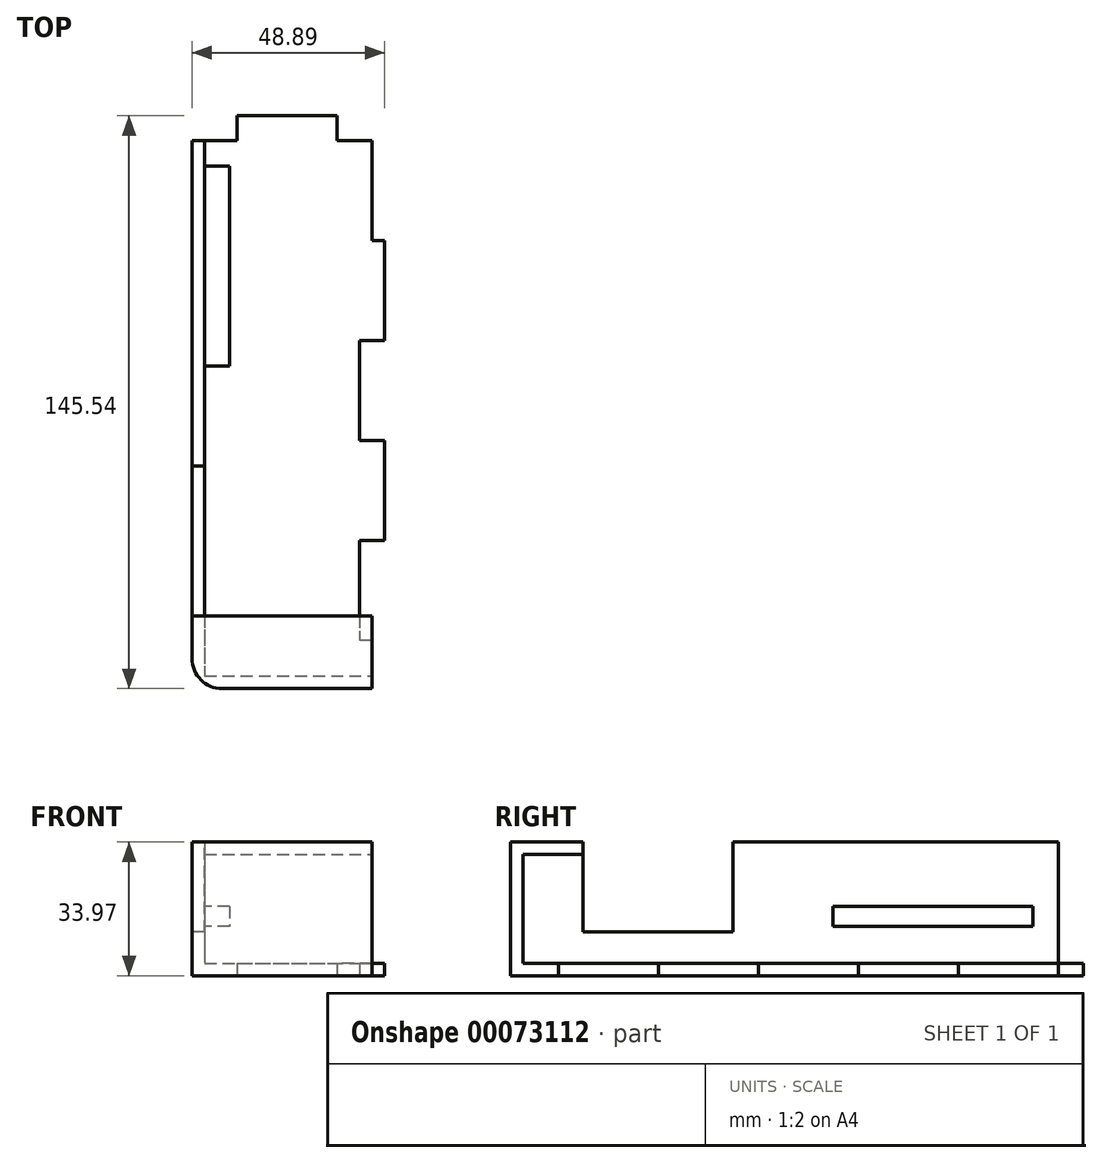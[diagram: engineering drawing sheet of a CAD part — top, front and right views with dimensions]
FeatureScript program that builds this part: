
annotation { "Feature Type Name" : "Feature", "Feature Type Description" : "" }
export const myFeature = defineFeature(function(context is Context, id is Id, definition is map)
    precondition{}
    {
        {
            var Q0;
            Q0=qCreatedBy(makeId("Top.planeOp"),FACE);
            var sketch = newSketch(context, id + "F0", { "sketchPlane" : qUnion([Q0])});
            skLineSegment(sketch, "E0.bottom", {"start": v(-32.54, 107.25) * mm, "end": v(-21.11, 107.25) * mm});
            skLineSegment(sketch, "E0.top", {"start": v(-32.54, -31.94) * mm, "end": v(13.18, -31.94) * mm});
            skLineSegment(sketch, "E0.left", {"start": v(-32.54, 107.25) * mm, "end": v(-32.54, -31.94) * mm});
            skLineSegment(sketch, "E1.bottom", {"start": v(13.18, 107.25) * mm, "end": v(10, 107.25) * mm});
            skLineSegment(sketch, "E1.top", {"start": v(13.18, 81.85) * mm, "end": v(10, 81.85) * mm});
            skLineSegment(sketch, "E2.0.1.0", {"start": v(13.18, 56.45) * mm, "end": v(10, 56.45) * mm});
            skLineSegment(sketch, "E2.0.1.1", {"start": v(10, 56.45) * mm, "end": v(10, 31.05) * mm});
            skLineSegment(sketch, "E2.0.1.2", {"start": v(13.18, 31.05) * mm, "end": v(10, 31.05) * mm});
            skLineSegment(sketch, "E2.0.2.0", {"start": v(13.18, 5.65) * mm, "end": v(10, 5.65) * mm});
            skLineSegment(sketch, "E2.0.2.1", {"start": v(10, 5.65) * mm, "end": v(10, -19.75) * mm});
            skLineSegment(sketch, "E2.0.2.2", {"start": v(13.18, -19.75) * mm, "end": v(10, -19.75) * mm});
            skLineSegment(sketch, "E2.direction1", {"start": v(10, 94.55) * mm, "end": v(35.4, 94.55) * mm, "construction": true});
            skLineSegment(sketch, "E2.direction2", {"start": v(10, 94.55) * mm, "end": v(10, 43.75) * mm, "construction": true});
            skLineSegment(sketch, "E3.bottom", {"start": v(13.18, 81.85) * mm, "end": v(16.35, 81.85) * mm});
            skLineSegment(sketch, "E3.top", {"start": v(13.18, 56.45) * mm, "end": v(16.35, 56.45) * mm});
            skLineSegment(sketch, "E3.right", {"start": v(16.35, 81.85) * mm, "end": v(16.35, 56.45) * mm});
            skLineSegment(sketch, "E4.0.1.0", {"start": v(13.18, 31.05) * mm, "end": v(16.35, 31.05) * mm});
            skLineSegment(sketch, "E4.0.1.1", {"start": v(16.35, 31.05) * mm, "end": v(16.35, 5.65) * mm});
            skLineSegment(sketch, "E4.0.1.2", {"start": v(13.18, 5.65) * mm, "end": v(16.35, 5.65) * mm});
            skLineSegment(sketch, "E4.direction1", {"start": v(13.18, 81.85) * mm, "end": v(38.58, 81.85) * mm, "construction": true});
            skLineSegment(sketch, "E4.direction2", {"start": v(13.18, 81.85) * mm, "end": v(13.18, 31.05) * mm, "construction": true});
            skLineSegment(sketch, "E5", {"start": v(13.18, 107.25) * mm, "end": v(13.18, 81.85) * mm});
            skLineSegment(sketch, "E6", {"start": v(13.18, -31.94) * mm, "end": v(13.18, -19.75) * mm});
            skLineSegment(sketch, "E7.top", {"start": v(-21.11, 113.6) * mm, "end": v(4.29, 113.6) * mm});
            skLineSegment(sketch, "E7.left", {"start": v(-21.11, 107.25) * mm, "end": v(-21.11, 113.6) * mm});
            skLineSegment(sketch, "E7.right", {"start": v(4.29, 107.25) * mm, "end": v(4.29, 113.6) * mm});
            skLineSegment(sketch, "E8.trimOffspring", {"start": v(4.29, 107.25) * mm, "end": v(13.18, 107.25) * mm});
            skSolve(sketch);
        }
        {
            var Q0;
            Q0=makeQuery(id+"F0.imprint","IMPRINT",FACE,{"disambiguationData":[TD([[makeQuery(id+"F0.imprint","IMPRINT",EDGE,{"derivedFrom":sQuery(id+"F0.wireOp",EDGE,"E0.bottom")}),-1.0]])]});
            extrude(context, id + "F1", {"entities" : qUnion([Q0]), "depth" : 3.17 * mm});
        }
        {
            var Q0;
            Q0=makeQuery(id+"F1.opExtrude","CAP_FACE",FACE,{"disambiguationData":[OSD([sQuery(id+"F0.wireOp",EDGE,"E0.bottom"),sQuery(id+"F0.wireOp",EDGE,"E0.top"),sQuery(id+"F0.wireOp",EDGE,"E0.left"),sQuery(id+"F0.wireOp",EDGE,"E1.top"),sQuery(id+"F0.wireOp",EDGE,"E1.right"),sQuery(id+"F0.wireOp",EDGE,"E2.0.1.0"),sQuery(id+"F0.wireOp",EDGE,"E2.0.1.1"),sQuery(id+"F0.wireOp",EDGE,"E2.0.1.2"),sQuery(id+"F0.wireOp",EDGE,"E2.0.2.0"),sQuery(id+"F0.wireOp",EDGE,"E2.0.2.1"),sQuery(id+"F0.wireOp",EDGE,"E2.0.2.2"),sQuery(id+"F0.wireOp",EDGE,"E2.0.3.0"),sQuery(id+"F0.wireOp",EDGE,"E2.0.3.1"),sQuery(id+"F0.wireOp",EDGE,"E3.bottom"),sQuery(id+"F0.wireOp",EDGE,"E3.top"),sQuery(id+"F0.wireOp",EDGE,"E3.right"),sQuery(id+"F0.wireOp",EDGE,"E4.0.1.0"),sQuery(id+"F0.wireOp",EDGE,"E4.0.1.1"),sQuery(id+"F0.wireOp",EDGE,"E4.0.1.2"),sQuery(id+"F0.wireOp",EDGE,"E4.0.2.0"),sQuery(id+"F0.wireOp",EDGE,"E4.0.2.1"),sQuery(id+"F0.wireOp",EDGE,"E4.0.2.2"),sQuery(id+"F0.wireOp",EDGE,"pYJ3T49I-Cm0M-1mBg-DGMC-QoNwpn64H0FC"),sQuery(id+"F0.wireOp",EDGE,"ms7zWnSc-LKju-jYRc-7B30-AOrHfCOUoyog")])],"isStart":false});
            var sketch = newSketch(context, id + "F2", { "sketchPlane" : qUnion([Q0])});
            skLineSegment(sketch, "E9.0", {"start": v(-29.37, -28.76) * mm, "end": v(13.18, -28.76) * mm});
            skLineSegment(sketch, "E9.1", {"start": v(-29.37, 107.25) * mm, "end": v(-29.37, -28.76) * mm});
            skSolve(sketch);
        }
        {
            var Q0;
            {var subQ2=sQuery(id+"F2.wireOp",EDGE,"E9.1");Q0=makeQuery(id+"F2.imprint","IMPRINT",FACE,{"disambiguationData":[TD([[makeQuery(id+"F2.imprint","IMPRINT",EDGE,{"derivedFrom":subQ2}),-1.0]])]});}
            extrude(context, id + "F3", {"entities" : qUnion([Q0]), "operationType" : NewBodyOperationType.ADD, "depth" : 30.8 * mm});
        }
        {
            var Q0;
            Q0=makeQuery(id+"F3.opExtrude","CAP_FACE",FACE,{"disambiguationData":[OSD([sQuery(id+"F0.wireOp",EDGE,"E0.bottom"),sQuery(id+"F0.wireOp",EDGE,"E0.top"),sQuery(id+"F0.wireOp",EDGE,"E0.left"),sQuery(id+"F0.wireOp",EDGE,"pYJ3T49I-Cm0M-1mBg-DGMC-QoNwpn64H0FC"),sQuery(id+"F2.wireOp",EDGE,"E9.0"),sQuery(id+"F2.wireOp",EDGE,"E9.1")])],"isStart":false});
            var sketch = newSketch(context, id + "F4", { "sketchPlane" : qUnion([Q0])});
            skLineSegment(sketch, "E10.bottom", {"start": v(13.18, -28.76) * mm, "end": v(-29.37, -28.76) * mm});
            skLineSegment(sketch, "E10.top", {"start": v(13.18, -13.52) * mm, "end": v(-29.37, -13.52) * mm});
            skLineSegment(sketch, "E10.left", {"start": v(13.18, -28.76) * mm, "end": v(13.18, -13.52) * mm});
            skLineSegment(sketch, "E10.right", {"start": v(-29.37, -28.76) * mm, "end": v(-29.37, -13.52) * mm});
            skSolve(sketch);
        }
        {
            var Q0;
            Q0=makeQuery(id+"F4.imprint","IMPRINT",FACE,{"disambiguationData":[TD([[makeQuery(id+"F4.imprint","IMPRINT",EDGE,{"derivedFrom":sQuery(id+"F4.wireOp",EDGE,"E10.bottom")}),1.0]])]});
            extrude(context, id + "F5", {"entities" : qUnion([Q0]), "operationType" : NewBodyOperationType.ADD, "oppositeDirection" : true, "depth" : 3.17 * mm});
        }
        {
            var Q0;
            {var subQ0=sQuery(id+"F0.wireOp",EDGE,"E0.left");Q0=makeQuery(id+"F3.boolean.opBoolean","MERGE",FACE,{"derivedFrom":[makeQuery(id+"F1.opExtrude","SWEPT_FACE",FACE,{"disambiguationData":[OSD([subQ0])]}),makeQuery(id+"F3.opExtrude","SWEPT_FACE",FACE,{"disambiguationData":[OSD([subQ0])]})]});}
            var sketch = newSketch(context, id + "F6", { "sketchPlane" : qUnion([Q0])});
            skLineSegment(sketch, "E11.bottom", {"start": v(13.52, 33.97) * mm, "end": v(-24.58, 33.97) * mm});
            skLineSegment(sketch, "E11.top", {"start": v(13.52, 11.11) * mm, "end": v(-24.58, 11.11) * mm});
            skLineSegment(sketch, "E11.left", {"start": v(13.52, 33.97) * mm, "end": v(13.52, 11.11) * mm});
            skLineSegment(sketch, "E11.right", {"start": v(-24.58, 33.97) * mm, "end": v(-24.58, 11.11) * mm});
            skSolve(sketch);
        }
        {
            var Q0;
            Q0=makeQuery(id+"F6.imprint","IMPRINT",FACE,{"disambiguationData":[TD([[makeQuery(id+"F6.imprint","IMPRINT",EDGE,{"derivedFrom":sQuery(id+"F6.wireOp",EDGE,"E11.bottom")}),-1.0]])]});
            extrude(context, id + "F7", {"entities" : qUnion([Q0]), "operationType" : NewBodyOperationType.REMOVE, "endBound" : BoundingType.THROUGH_ALL, "oppositeDirection" : true, "depth" : 25.4 * mm});
        }
        {
            var Q0;
            Q0=makeQuery(id+"F3.opExtrude","SWEPT_FACE",FACE,{"disambiguationData":[OSD([sQuery(id+"F2.wireOp",EDGE,"E9.1")])]});
            var sketch = newSketch(context, id + "F8", { "sketchPlane" : qUnion([Q0])});
            skLineSegment(sketch, "E12.bottom", {"start": v(49.98, 17.62) * mm, "end": v(100.78, 17.62) * mm});
            skLineSegment(sketch, "E12.top", {"start": v(49.98, 12.54) * mm, "end": v(100.78, 12.54) * mm});
            skLineSegment(sketch, "E12.left", {"start": v(49.98, 17.62) * mm, "end": v(49.98, 12.54) * mm});
            skLineSegment(sketch, "E12.right", {"start": v(100.78, 17.62) * mm, "end": v(100.78, 12.54) * mm});
            skSolve(sketch);
        }
        {
            var Q0;
            Q0=makeQuery(id+"F8.imprint","IMPRINT",FACE,{"disambiguationData":[TD([[makeQuery(id+"F8.imprint","IMPRINT",EDGE,{"derivedFrom":sQuery(id+"F8.wireOp",EDGE,"E12.bottom")}),-1.0]])]});
            extrude(context, id + "F9", {"entities" : qUnion([Q0]), "operationType" : NewBodyOperationType.ADD, "depth" : 6.35 * mm});
        }
        {
            var Q0;
            {var subQ0=sQuery(id+"F0.wireOp",EDGE,"E0.left");var subQ1=sQuery(id+"F0.wireOp",EDGE,"E0.top");Q0=makeQuery(id+"F3.boolean.opBoolean","MERGE",EDGE,{"derivedFrom":[makeQuery(id+"F1.opExtrude","SWEPT_EDGE",EDGE,{"disambiguationData":[OSD([subQ1,subQ0])]}),makeQuery(id+"F3.opExtrude","SWEPT_EDGE",EDGE,{"disambiguationData":[OSD([subQ1,subQ0])]})]});}
            fillet(context, id + "F10", {"entities" : qUnion([Q0]), "radius" : 7.62 * mm, "tangentPropagation" : true, "allowEdgeOverflow" : false});
        }
    });
